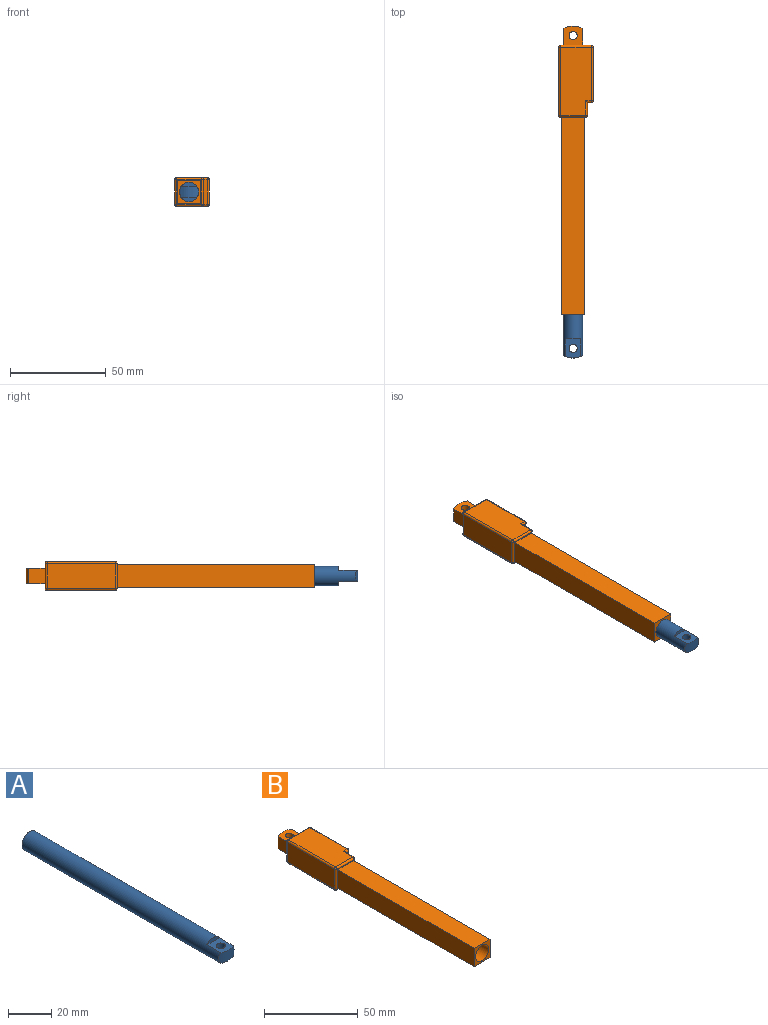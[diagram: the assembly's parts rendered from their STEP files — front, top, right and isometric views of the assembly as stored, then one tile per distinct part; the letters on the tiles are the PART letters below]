
ASSEMBLY  parts=2 mates=1
PART A: 8 faces, bbox 10x130x10 mm
  f0: cylinder r=5mm len=129.15mm, axis (0,1,0), area 3881.4mm2, adj f1,f2,f3,f4,f5,f6
  f1: plane 10x8.07mm, normal (0,0,-1), area 64mm2, adj f0,f4,f6,f7
  f2: plane 10x8.07mm, normal (0,0,1), area 64mm2, adj f0,f3,f6,f7
  f3: plane 8.07x2.05mm, normal (0,-1,0), area 11.6mm2, adj f0,f2
  f4: plane 8.07x2.05mm, normal (0,-1,0), area 11.6mm2, adj f0,f1
  f5: plane 10x10mm, normal (0,1,0), area 78.5mm2, adj f0
  f6: cylinder r=10mm len=10mm, axis (0,0,1), area 57.7mm2, adj f0,f1,f2
  f7: cylinder r=2.15mm len=5.9mm, axis (0,0,1), area 79.7mm2, adj f1,f2
PART B: 48 faces, bbox 18x150.5x15 mm
  f0: plane 16x13mm, normal (0,1,0), area 128mm2, adj f16,f18,f19,f20,f21,f22,f25,f26
  f1: plane 103x12mm, normal (-1,0,0), area 1236mm2, adj f2,f4,f5,f7
  f2: plane 12x12mm, normal (0,-1,0), area 65.5mm2, adj f1,f3,f4,f5,f13
  f3: plane 103x12mm, normal (1,0,0), area 1236mm2, adj f2,f4,f5,f7
  f4: plane 103x12mm, normal (0,0,1), area 1236mm2, adj f1,f2,f3,f7
  f5: plane 103x12mm, normal (0,0,-1), area 1236mm2, adj f1,f2,f3,f7
  f6: plane 35.5x13mm, normal (-1,0,0), area 461.5mm2, adj f26,f32,f35,f36
  f7: plane 13x13mm, normal (0,-1,0), area 25mm2, adj f1,f3,f4,f5,f36,f41,f44,f47
  f8: plane 13x6.5mm, normal (1,0,0), area 84.5mm2, adj f9,f42,f43,f47
  f9: plane 13x2mm, normal (0,-1,0), area 26mm2, adj f8,f29,f38,f39
  f10: plane 28x13mm, normal (1,0,0), area 364mm2, adj f21,f28,f29,f30
  f11: plane 35.5x16mm, normal (0,0,1), area 545.5mm2, adj f22,f28,f32,f38,f41,f42
  f12: plane 35.5x16mm, normal (0,0,-1), area 545.5mm2, adj f25,f30,f35,f39,f43,f44
  f13: cylinder r=5mm len=120mm, axis (0,-1,0), area 3769.9mm2, adj f2,f14
  f14: plane 10x10mm, normal (0,-1,0), area 78.5mm2, adj f13
  f15: cylinder r=10mm len=10mm, axis (0,0,-1), area 83.8mm2, adj f16,f18,f19,f20
  f16: plane 8.66x8mm, normal (-1,0,0), area 69.3mm2, adj f0,f15,f19,f20
  f17: cylinder r=2.15mm len=8mm, axis (0,0,-1), area 108.1mm2, adj f19,f20
  f18: plane 8.66x8mm, normal (1,0,0), area 69.3mm2, adj f0,f15,f19,f20
  f19: plane 10x10mm, normal (0,0,1), area 81.1mm2, adj f0,f15,f16,f17,f18
  f20: plane 10x10mm, normal (0,0,-1), area 81.1mm2, adj f0,f15,f16,f17,f18
  f21: cylinder r=1mm len=13mm, axis (0,0,-1), area 20.4mm2, adj f0,f10,f23,f24
  f22: cylinder r=1mm len=16mm, axis (1,0,0), area 25.1mm2, adj f0,f11,f23,f27
  f23: sphere r=1mm, area 1.6mm2, adj f21,f22,f28
  f24: sphere r=1mm, area 1.6mm2, adj f21,f25,f30
  f25: cylinder r=1mm len=16mm, axis (-1,0,0), area 25.1mm2, adj f0,f12,f24,f31
  f26: cylinder r=1mm len=13mm, axis (0,0,1), area 20.4mm2, adj f0,f6,f27,f31
  f27: sphere r=1mm, area 1.6mm2, adj f22,f26,f32
  f28: cylinder r=1mm len=28mm, axis (0,-1,0), area 44mm2, adj f10,f11,f23,f33
  f29: cylinder r=1mm len=13mm, axis (0,0,1), area 20.4mm2, adj f9,f10,f33,f34
  f30: cylinder r=1mm len=28mm, axis (0,1,0), area 44mm2, adj f10,f12,f24,f34
  f31: sphere r=1mm, area 1.6mm2, adj f25,f26,f35
  f32: cylinder r=1mm len=35.5mm, axis (0,1,0), area 55.8mm2, adj f6,f11,f27,f37
  f33: sphere r=1mm, area 1.6mm2, adj f28,f29,f38
  f34: sphere r=1mm, area 1.6mm2, adj f29,f30,f39
  f35: cylinder r=1mm len=35.5mm, axis (0,-1,0), area 55.8mm2, adj f6,f12,f31,f40
  f36: cylinder r=1mm len=13mm, axis (0,0,-1), area 20.4mm2, adj f6,f7,f37,f40
  f37: sphere r=1mm, area 1.6mm2, adj f32,f36,f41
  f38: cylinder r=1mm len=3mm, axis (-1,0,0), area 3.7mm2, adj f9,f11,f33,f42
  f39: cylinder r=1mm len=3mm, axis (1,0,0), area 3.7mm2, adj f9,f12,f34,f43
  f40: sphere r=1mm, area 1.6mm2, adj f35,f36,f44
  f41: cylinder r=1mm len=13mm, axis (-1,0,0), area 20.4mm2, adj f7,f11,f37,f45
  f42: cylinder r=1mm len=7.5mm, axis (0,-1,0), area 10.8mm2, adj f8,f11,f38,f45
  f43: cylinder r=1mm len=7.5mm, axis (0,1,0), area 10.8mm2, adj f8,f12,f39,f46
  f44: cylinder r=1mm len=13mm, axis (1,0,0), area 20.4mm2, adj f7,f12,f40,f46
  f45: sphere r=1mm, area 1.6mm2, adj f41,f42,f47
  f46: sphere r=1mm, area 1.6mm2, adj f43,f44,f47
  f47: cylinder r=1mm len=13mm, axis (0,0,1), area 20.4mm2, adj f7,f8,f45,f46
PLACE A t=(-35.82,-22.12,1.71)mm
PLACE B t=(-5.82,0.72,1.71)mm fixed
MATE slider A.f0 <-> B.f13  axis (0,1,0) through (-5.82,37.88,1.71)mm
